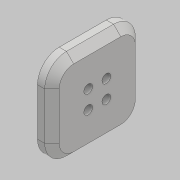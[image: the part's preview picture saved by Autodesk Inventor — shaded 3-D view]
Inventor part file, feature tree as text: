
AUTODESK INVENTOR PART (.ipt)
format: ipt  version: 2018 (Build 220112000, 112)  size: 134,144 bytes
history: native  units: mm
features: sketch x3, hole x2, other x1, extrude x1, fillet x1, chamfer x1, projected_geometry x1
ambient origin geometry x8: Origin, YZ Plane, XZ Plane, XY Plane, X Axis, Y Axis, Z Axis, Center Point
bodies: Body1 (feature_tree)
feature tree (10):
  other  "實體1"
  extrude  "擠出1"  Depth=125.0mm
  fillet  "圓角1"  Radius=125.0mm
  chamfer  "倒角1"  Distance=20.0mm
  hole  "孔1"  [1 undecoded]
  hole  "孔2"  [1 undecoded]
  sketch  "草圖1"
  sketch  "草圖2"
  sketch  "草圖3"
  projected_geometry  "投影迴路1"
note: 2 required parameter values undecoded (feature->parameter linkage not recoverable at this tier; creation-order binding heuristic only, values carry confidence <= 0.55)
